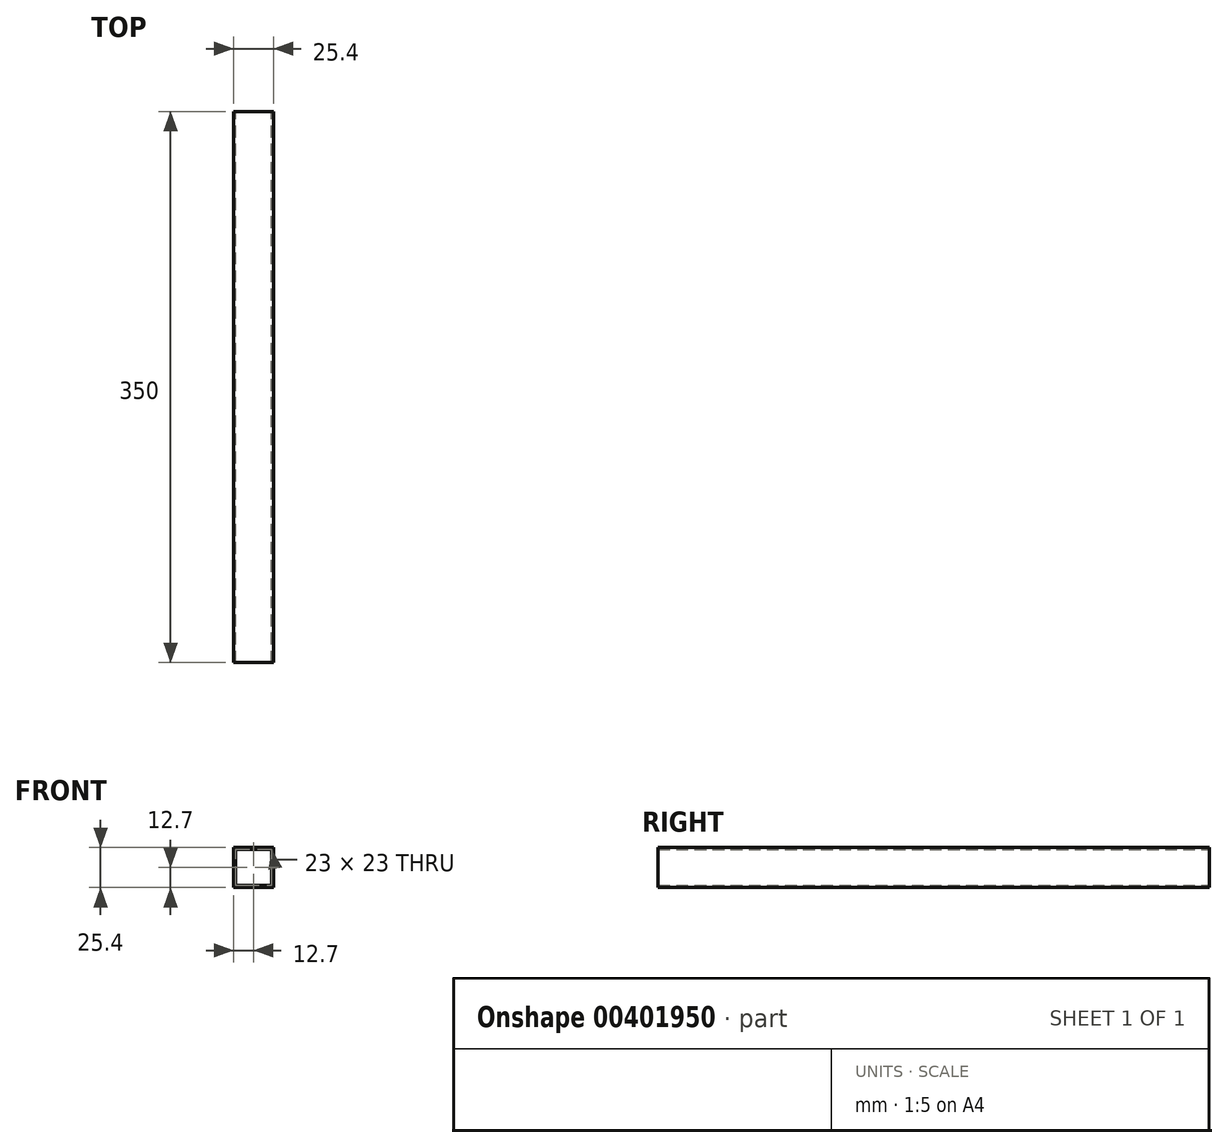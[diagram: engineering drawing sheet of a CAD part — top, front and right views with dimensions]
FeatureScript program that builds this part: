
annotation { "Feature Type Name" : "Feature", "Feature Type Description" : "" }
export const myFeature = defineFeature(function(context is Context, id is Id, definition is map)
    precondition{}
    {
        {
            var Q0;
            Q0=qCreatedBy(makeId("Front.planeOp"),FACE);
            var sketch = newSketch(context, id + "F0", { "sketchPlane" : qUnion([Q0])});
            skLineSegment(sketch, "E0.bottom", {"start": v(-12.7, 12.7) * mm, "end": v(12.7, 12.7) * mm});
            skLineSegment(sketch, "E0.top", {"start": v(-12.7, -12.7) * mm, "end": v(12.7, -12.7) * mm});
            skLineSegment(sketch, "E0.left", {"start": v(-12.7, 12.7) * mm, "end": v(-12.7, -12.7) * mm});
            skLineSegment(sketch, "E0.right", {"start": v(12.7, 12.7) * mm, "end": v(12.7, -12.7) * mm});
            skLineSegment(sketch, "E1", {"start": v(0, 0) * mm, "end": v(0, 12.7) * mm, "construction": true});
            skLineSegment(sketch, "E2", {"start": v(0, 0) * mm, "end": v(-12.7, 0) * mm, "construction": true});
            skLineSegment(sketch, "E3.0", {"start": v(-11.5, -11.5) * mm, "end": v(11.5, -11.5) * mm});
            skLineSegment(sketch, "E3.1", {"start": v(-11.5, 11.5) * mm, "end": v(-11.5, -11.5) * mm});
            skLineSegment(sketch, "E3.2", {"start": v(-11.5, 11.5) * mm, "end": v(11.5, 11.5) * mm});
            skLineSegment(sketch, "E3.3", {"start": v(11.5, 11.5) * mm, "end": v(11.5, -11.5) * mm});
            skSolve(sketch);
        }
        {
            var Q0;
            Q0=qSketchRegion(id+"F0",true);
            var Q1;
            Q1=qConstructionFilter(qBodyType(qCreatedBy(id+"F0",EDGE),BodyType.WIRE),ConstructionObject.NO);
            extrude(context, id + "F1", {"entities" : qUnion([Q0]), "surfaceEntities" : qUnion([Q1]), "endBound" : BoundingType.SYMMETRIC, "depth" : 350 * mm});
        }
        {
            var Q0;
            Q0=qCreatedBy(makeId("Top.planeOp"),FACE);
            var sketch = newSketch(context, id + "F2", { "sketchPlane" : qUnion([Q0])});
            skLineSegment(sketch, "E4.0.0", {"start": v(12.7, 175) * mm, "end": v(-12.7, 175) * mm});
            skLineSegment(sketch, "E4.0.1", {"start": v(-12.7, 175) * mm, "end": v(-12.7, -175) * mm});
            skLineSegment(sketch, "E4.0.2", {"start": v(-12.7, -175) * mm, "end": v(12.7, -175) * mm});
            skLineSegment(sketch, "E4.0.3", {"start": v(12.7, -175) * mm, "end": v(12.7, 175) * mm});
            skSolve(sketch);
        }
    });
